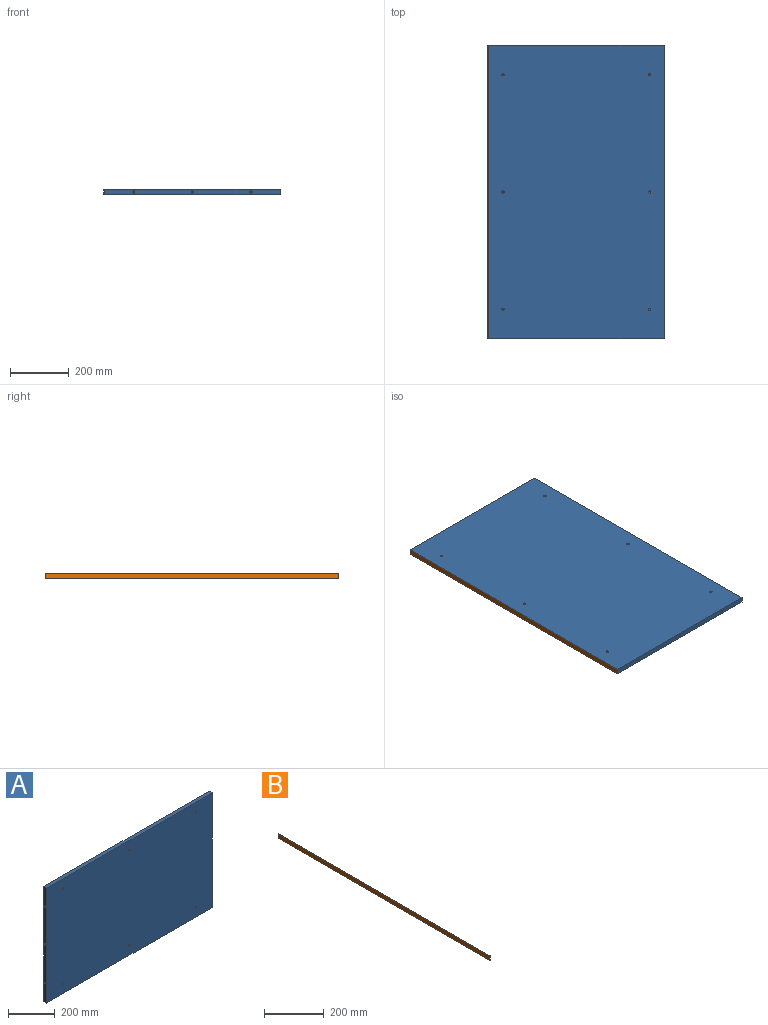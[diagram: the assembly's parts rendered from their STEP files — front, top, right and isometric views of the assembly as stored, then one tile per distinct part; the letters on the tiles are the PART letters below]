
ASSEMBLY  parts=2 mates=1
PART A: 30 faces, bbox 1000x18x600 mm
  f0: plane 1000x18mm, normal (0,0,1), area 18000mm2, adj f1,f3,f4,f5
  f1: plane 600x18mm, normal (-1,0,0), area 10649.2mm2, adj f0,f2,f4,f5,f19,f21,f23
  f2: plane 1000x18mm, normal (0,0,-1), area 18000mm2, adj f1,f3,f4,f5
  f3: plane 600x18mm, normal (1,0,0), area 10649.2mm2, adj f0,f2,f4,f5,f25,f27,f29
  f4: plane 1000x600mm, normal (0,-1,0), area 599698.4mm2, adj f0,f1,f2,f3,f7,f9,f11,f13
  f5: plane 1000x600mm, normal (0,1,0), area 600000mm2, adj f0,f1,f2,f3
  f6: cone r=0mm half-angle=59deg, axis (0,-1,0), area 58.6mm2, adj f7
  f7: cylinder r=4mm len=12mm, axis (0,-1,0), area 301.6mm2, adj f4,f6
  f8: cone r=0mm half-angle=59deg, axis (0,-1,0), area 58.6mm2, adj f9
  f9: cylinder r=4mm len=12mm, axis (0,-1,0), area 301.6mm2, adj f4,f8
  f10: cone r=0mm half-angle=59deg, axis (0,-1,0), area 58.6mm2, adj f11
  f11: cylinder r=4mm len=12mm, axis (0,-1,0), area 301.6mm2, adj f4,f10
  f12: cone r=0mm half-angle=59deg, axis (0,-1,0), area 58.6mm2, adj f13
  f13: cylinder r=4mm len=12mm, axis (0,-1,0), area 301.6mm2, adj f4,f12
  f14: cone r=0mm half-angle=59deg, axis (0,-1,0), area 58.6mm2, adj f15
  f15: cylinder r=4mm len=12mm, axis (0,-1,0), area 301.6mm2, adj f4,f14
  f16: cone r=0mm half-angle=59deg, axis (0,-1,0), area 58.6mm2, adj f17
  f17: cylinder r=4mm len=12mm, axis (0,-1,0), area 301.6mm2, adj f4,f16
  f18: cone r=0mm half-angle=59deg, axis (-1,0,0), area 58.6mm2, adj f19
  f19: cylinder r=4mm len=18mm, axis (-1,0,0), area 452.4mm2, adj f1,f18
  f20: cone r=0mm half-angle=59deg, axis (-1,0,0), area 58.6mm2, adj f21
  f21: cylinder r=4mm len=18mm, axis (-1,0,0), area 452.4mm2, adj f1,f20
  f22: cone r=0mm half-angle=59deg, axis (-1,0,0), area 58.6mm2, adj f23
  f23: cylinder r=4mm len=18mm, axis (-1,0,0), area 452.4mm2, adj f1,f22
  f24: cone r=0mm half-angle=59deg, axis (1,0,0), area 58.6mm2, adj f25
  f25: cylinder r=4mm len=18mm, axis (1,0,0), area 452.4mm2, adj f3,f24
  f26: cone r=0mm half-angle=59deg, axis (1,0,0), area 58.6mm2, adj f27
  f27: cylinder r=4mm len=18mm, axis (1,0,0), area 452.4mm2, adj f3,f26
  f28: cone r=0mm half-angle=59deg, axis (1,0,0), area 58.6mm2, adj f29
  f29: cylinder r=4mm len=18mm, axis (1,0,0), area 452.4mm2, adj f3,f28
PART B: 8 faces, bbox 2x1000x18 mm
  f0: plane 1000x18mm, normal (1,0,0), area 18000mm2, adj f1,f5,f6,f7
  f1: plane 1000x1.2mm, normal (0,0,1), area 1200mm2, adj f0,f2,f6,f7
  f2: cylinder r=0.8mm len=1000mm, axis (0,1,0), area 1256.6mm2, adj f1,f3,f6,f7
  f3: plane 1000x16.4mm, normal (-1,0,0), area 16400mm2, adj f2,f4,f6,f7
  f4: cylinder r=0.8mm len=1000mm, axis (0,1,0), area 1256.6mm2, adj f3,f5,f6,f7
  f5: plane 1000x1.2mm, normal (0,0,-1), area 1200mm2, adj f0,f4,f6,f7
  f6: plane 18x2mm, normal (0,-1,0), area 35.7mm2, adj f0,f1,f2,f3,f4,f5
  f7: plane 18x2mm, normal (0,1,0), area 35.7mm2, adj f0,f1,f2,f3,f4,f5
PLACE A rot(axis=(-0.58,0.58,-0.58),120deg) t=(-36.58,-92.74,-41.03)mm
PLACE B t=(-336.58,407.26,-41.03)mm
MATE planar B.f0 <-> A.f2  axis (1,0,0) through (-336.58,407.26,-32.03)mm
